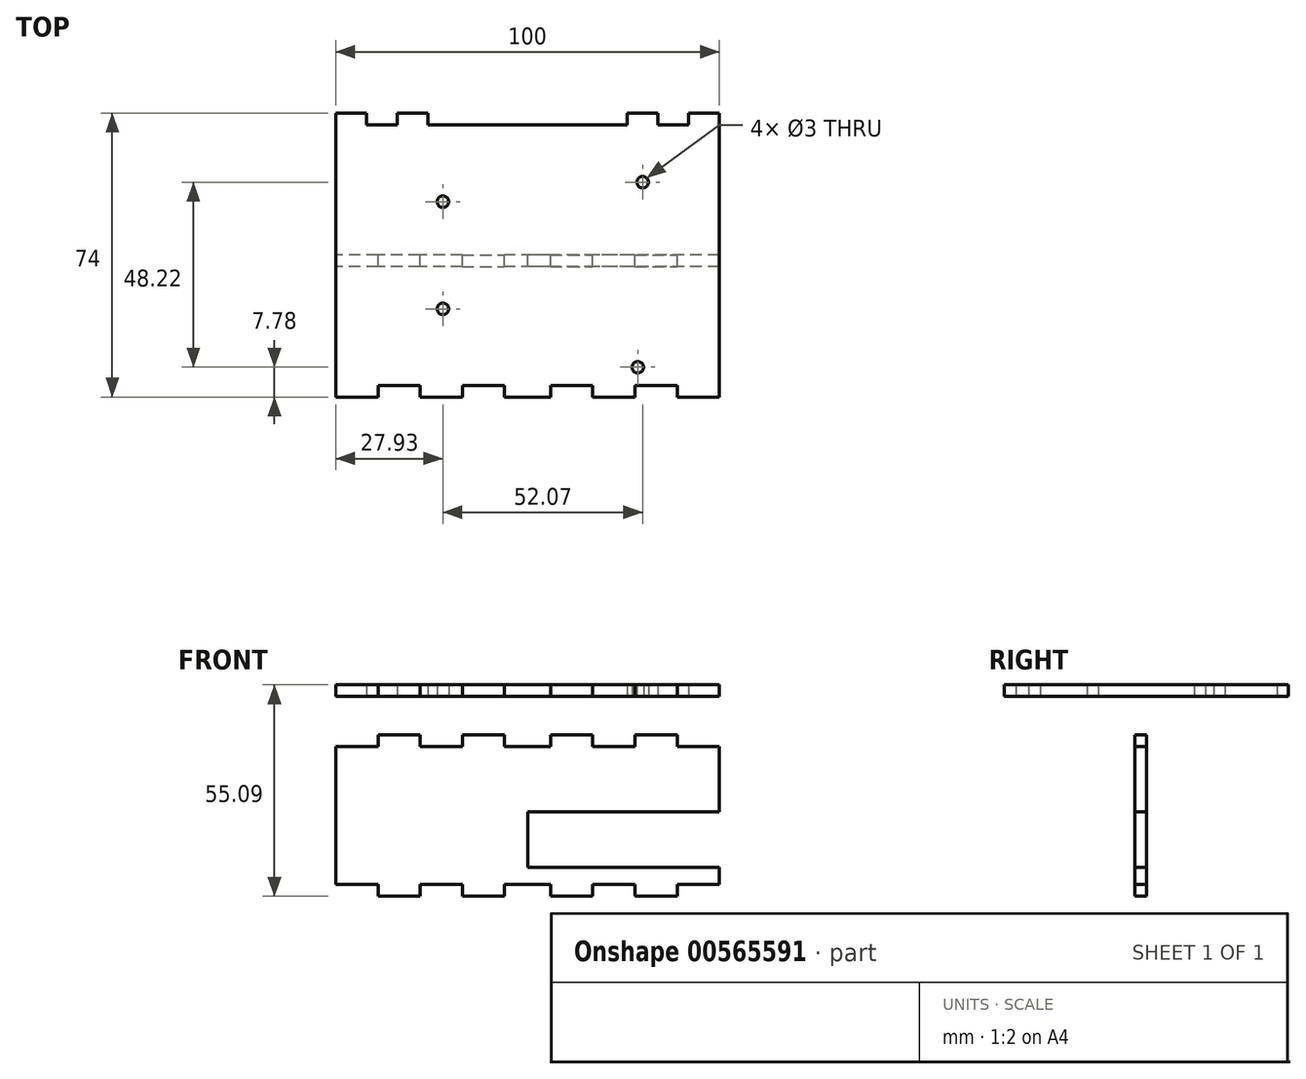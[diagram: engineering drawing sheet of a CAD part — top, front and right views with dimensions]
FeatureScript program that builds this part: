
annotation { "Feature Type Name" : "Feature", "Feature Type Description" : "" }
export const myFeature = defineFeature(function(context is Context, id is Id, definition is map)
    precondition{}
    {
        {
            var Q0;
            Q0=qCreatedBy(makeId("Top.planeOp"),FACE);
            var sketch = newSketch(context, id + "F0", { "sketchPlane" : qUnion([Q0])});
            skLineSegment(sketch, "E0.bottom", {"start": v(50, -37) * mm, "end": v(39, -37) * mm});
            skLineSegment(sketch, "E0.top", {"start": v(50, 37) * mm, "end": v(42, 37) * mm});
            skLineSegment(sketch, "E0.left", {"start": v(50, -37) * mm, "end": v(50, 37) * mm});
            skLineSegment(sketch, "E0.right", {"start": v(-50, -37) * mm, "end": v(-50, 37) * mm});
            skPoint(sketch, "E0.middle", {"position": v(0, 0) * mm});
            skLineSegment(sketch, "E1.top", {"start": v(-42, 34) * mm, "end": v(-34, 34) * mm});
            skLineSegment(sketch, "E1.left", {"start": v(-42, 37) * mm, "end": v(-42, 34) * mm});
            skLineSegment(sketch, "E1.right", {"start": v(-34, 37) * mm, "end": v(-34, 34) * mm});
            skLineSegment(sketch, "E2.left", {"start": v(-26, 34) * mm, "end": v(-26, 37) * mm});
            skLineSegment(sketch, "E3.right", {"start": v(26, 34) * mm, "end": v(26, 37) * mm});
            skLineSegment(sketch, "E4.bottom", {"start": v(34, 34) * mm, "end": v(42, 34) * mm});
            skLineSegment(sketch, "E4.left", {"start": v(34, 34) * mm, "end": v(34, 37) * mm});
            skLineSegment(sketch, "E4.right", {"start": v(42, 34) * mm, "end": v(42, 37) * mm});
            skLineSegment(sketch, "E5.top", {"start": v(-39, -34) * mm, "end": v(-28, -34) * mm});
            skLineSegment(sketch, "E5.left", {"start": v(-39, -37) * mm, "end": v(-39, -34) * mm});
            skLineSegment(sketch, "E5.right", {"start": v(-28, -37) * mm, "end": v(-28, -34) * mm});
            skLineSegment(sketch, "E6.bottom", {"start": v(-17, -34) * mm, "end": v(-6, -34) * mm});
            skLineSegment(sketch, "E6.left", {"start": v(-17, -34) * mm, "end": v(-17, -37) * mm});
            skLineSegment(sketch, "E6.right", {"start": v(-6, -34) * mm, "end": v(-6, -37) * mm});
            skLineSegment(sketch, "E7.bottom", {"start": v(6, -34) * mm, "end": v(17, -34) * mm});
            skLineSegment(sketch, "E7.left", {"start": v(6, -34) * mm, "end": v(6, -37) * mm});
            skLineSegment(sketch, "E7.right", {"start": v(17, -34) * mm, "end": v(17, -37) * mm});
            skLineSegment(sketch, "E8.bottom", {"start": v(28, -34) * mm, "end": v(39, -34) * mm});
            skLineSegment(sketch, "E8.left", {"start": v(28, -34) * mm, "end": v(28, -37) * mm});
            skLineSegment(sketch, "E8.right", {"start": v(39, -34) * mm, "end": v(39, -37) * mm});
            skLineSegment(sketch, "E9.trimOffspring", {"start": v(28, -37) * mm, "end": v(17, -37) * mm});
            skLineSegment(sketch, "E10.trimOffspring", {"start": v(6, -37) * mm, "end": v(-6, -37) * mm});
            skLineSegment(sketch, "E11.trimOffspring", {"start": v(-17, -37) * mm, "end": v(-28, -37) * mm});
            skLineSegment(sketch, "E12.trimOffspring", {"start": v(-39, -37) * mm, "end": v(-50, -37) * mm});
            skLineSegment(sketch, "E13.trimOffspring", {"start": v(34, 37) * mm, "end": v(26, 37) * mm});
            skLineSegment(sketch, "E14.trimOffspring", {"start": v(-42, 37) * mm, "end": v(-50, 37) * mm});
            skLineSegment(sketch, "E15.trimOffspring", {"start": v(-26, 37) * mm, "end": v(-34, 37) * mm});
            skLineSegment(sketch, "E16", {"start": v(-26, 34) * mm, "end": v(26, 34) * mm});
            skCircle(sketch, "E17", {"center": v(-22.07, 13.92) * mm, "radius": 1.5 * mm});
            skCircle(sketch, "E18", {"center": v(30, 19) * mm, "radius": 1.5 * mm});
            skCircle(sketch, "E19", {"center": v(28.73, -29.22) * mm, "radius": 1.5 * mm});
            skCircle(sketch, "E20", {"center": v(-22.07, -14.02) * mm, "radius": 1.5 * mm});
            skSolve(sketch);
        }
        {
            var Q0;
            {var subQ6=sQuery(id+"F0.wireOp",EDGE,"E0.left");Q0=makeQuery(id+"F0.imprint","IMPRINT",FACE,{"disambiguationData":[TD([[makeQuery(id+"F0.imprint","IMPRINT",EDGE,{"derivedFrom":subQ6}),1.0]])]});}
            extrude(context, id + "F1", {"entities" : qUnion([Q0]), "depth" : 3 * mm, "offsetDistance" : 25 * mm});
        }
        {
            var Q0;
            Q0=qCreatedBy(makeId("Front.planeOp"),FACE);
            var sketch = newSketch(context, id + "F2", { "sketchPlane" : qUnion([Q0])});
            skLineSegment(sketch, "E21.top", {"start": v(-39, -52.09) * mm, "end": v(-28, -52.09) * mm});
            skLineSegment(sketch, "E21.left", {"start": v(-50, -13.09) * mm, "end": v(-50, -49.09) * mm});
            skLineSegment(sketch, "E21.right", {"start": v(50, -11.09) * mm, "end": v(50, -30.09) * mm});
            skLineSegment(sketch, "E22.top", {"start": v(-17, -10.09) * mm, "end": v(-6, -10.09) * mm});
            skLineSegment(sketch, "E22.left", {"start": v(-17, -10.09) * mm, "end": v(-17, -13.09) * mm});
            skLineSegment(sketch, "E22.right", {"start": v(-6, -10.09) * mm, "end": v(-6, -13.09) * mm});
            skLineSegment(sketch, "E23.bottom", {"start": v(6, -10.09) * mm, "end": v(17, -10.09) * mm});
            skLineSegment(sketch, "E23.left", {"start": v(6, -13.09) * mm, "end": v(6, -10.09) * mm});
            skLineSegment(sketch, "E23.right", {"start": v(17, -13.09) * mm, "end": v(17, -10.09) * mm});
            skLineSegment(sketch, "E24.bottom", {"start": v(28, -10.09) * mm, "end": v(39, -10.09) * mm});
            skLineSegment(sketch, "E24.left", {"start": v(28, -13.09) * mm, "end": v(28, -10.09) * mm});
            skLineSegment(sketch, "E24.right", {"start": v(39, -13.09) * mm, "end": v(39, -10.09) * mm});
            skLineSegment(sketch, "E25.top", {"start": v(50, -49.09) * mm, "end": v(39, -49.09) * mm});
            skLineSegment(sketch, "E25.right", {"start": v(39, -52.09) * mm, "end": v(39, -49.09) * mm});
            skLineSegment(sketch, "E26.bottom", {"start": v(28, -49.09) * mm, "end": v(17, -49.09) * mm});
            skLineSegment(sketch, "E26.left", {"start": v(28, -49.09) * mm, "end": v(28, -52.09) * mm});
            skLineSegment(sketch, "E26.right", {"start": v(17, -49.09) * mm, "end": v(17, -52.09) * mm});
            skLineSegment(sketch, "E27.bottom", {"start": v(6, -49.09) * mm, "end": v(-6, -49.09) * mm});
            skLineSegment(sketch, "E27.left", {"start": v(6, -49.09) * mm, "end": v(6, -52.09) * mm});
            skLineSegment(sketch, "E27.right", {"start": v(-6, -49.09) * mm, "end": v(-6, -52.09) * mm});
            skLineSegment(sketch, "E28.bottom", {"start": v(-17, -49.09) * mm, "end": v(-28, -49.09) * mm});
            skLineSegment(sketch, "E28.left", {"start": v(-17, -49.09) * mm, "end": v(-17, -52.09) * mm});
            skLineSegment(sketch, "E28.right", {"start": v(-28, -49.09) * mm, "end": v(-28, -52.09) * mm});
            skLineSegment(sketch, "E29.top", {"start": v(-50, -49.09) * mm, "end": v(-39, -49.09) * mm});
            skLineSegment(sketch, "E29.right", {"start": v(-39, -52.09) * mm, "end": v(-39, -49.09) * mm});
            skLineSegment(sketch, "E30.trimOffspring", {"start": v(28, -52.09) * mm, "end": v(39, -52.09) * mm});
            skLineSegment(sketch, "E31.trimOffspring", {"start": v(6, -52.09) * mm, "end": v(17, -52.09) * mm});
            skLineSegment(sketch, "E32.trimOffspring", {"start": v(-17, -52.09) * mm, "end": v(-6, -52.09) * mm});
            skLineSegment(sketch, "E33.trimOffspring", {"start": v(-6, -13.09) * mm, "end": v(6, -13.09) * mm});
            skLineSegment(sketch, "E34.trimOffspring", {"start": v(17, -13.09) * mm, "end": v(28, -13.09) * mm});
            skLineSegment(sketch, "E35.trimOffspring", {"start": v(39, -13.09) * mm, "end": v(39, -13.09) * mm});
            skLineSegment(sketch, "E36.bottom", {"start": v(50, -44.59) * mm, "end": v(0, -44.59) * mm});
            skLineSegment(sketch, "E36.top", {"start": v(50, -30.09) * mm, "end": v(0, -30.09) * mm});
            skLineSegment(sketch, "E36.right", {"start": v(0, -44.59) * mm, "end": v(0, -30.09) * mm});
            skLineSegment(sketch, "E37", {"start": v(39, -13.09) * mm, "end": v(50, -13.09) * mm});
            skLineSegment(sketch, "E38", {"start": v(-17, -13.09) * mm, "end": v(-28, -13.09) * mm});
            skLineSegment(sketch, "E39", {"start": v(-28, -13.09) * mm, "end": v(-28, -10.09) * mm});
            skLineSegment(sketch, "E40", {"start": v(-28, -10.09) * mm, "end": v(-39, -10.09) * mm});
            skLineSegment(sketch, "E41", {"start": v(-39, -10.09) * mm, "end": v(-39, -13.09) * mm});
            skLineSegment(sketch, "E42", {"start": v(-39, -13.09) * mm, "end": v(-50, -13.09) * mm});
            skLineSegment(sketch, "E43.trimOffspring", {"start": v(50, -44.59) * mm, "end": v(50, -49.09) * mm});
            skSolve(sketch);
        }
        {
            var Q0;
            Q0=makeQuery(id+"F2.imprint","IMPRINT",FACE,{"disambiguationData":[TD([[makeQuery(id+"F2.imprint","IMPRINT",EDGE,{"derivedFrom":sQuery(id+"F2.wireOp",EDGE,"E21.top")}),1.0]])]});
            extrude(context, id + "F3", {"entities" : qUnion([Q0]), "depth" : 3 * mm, "offsetDistance" : 25 * mm});
        }
    });
